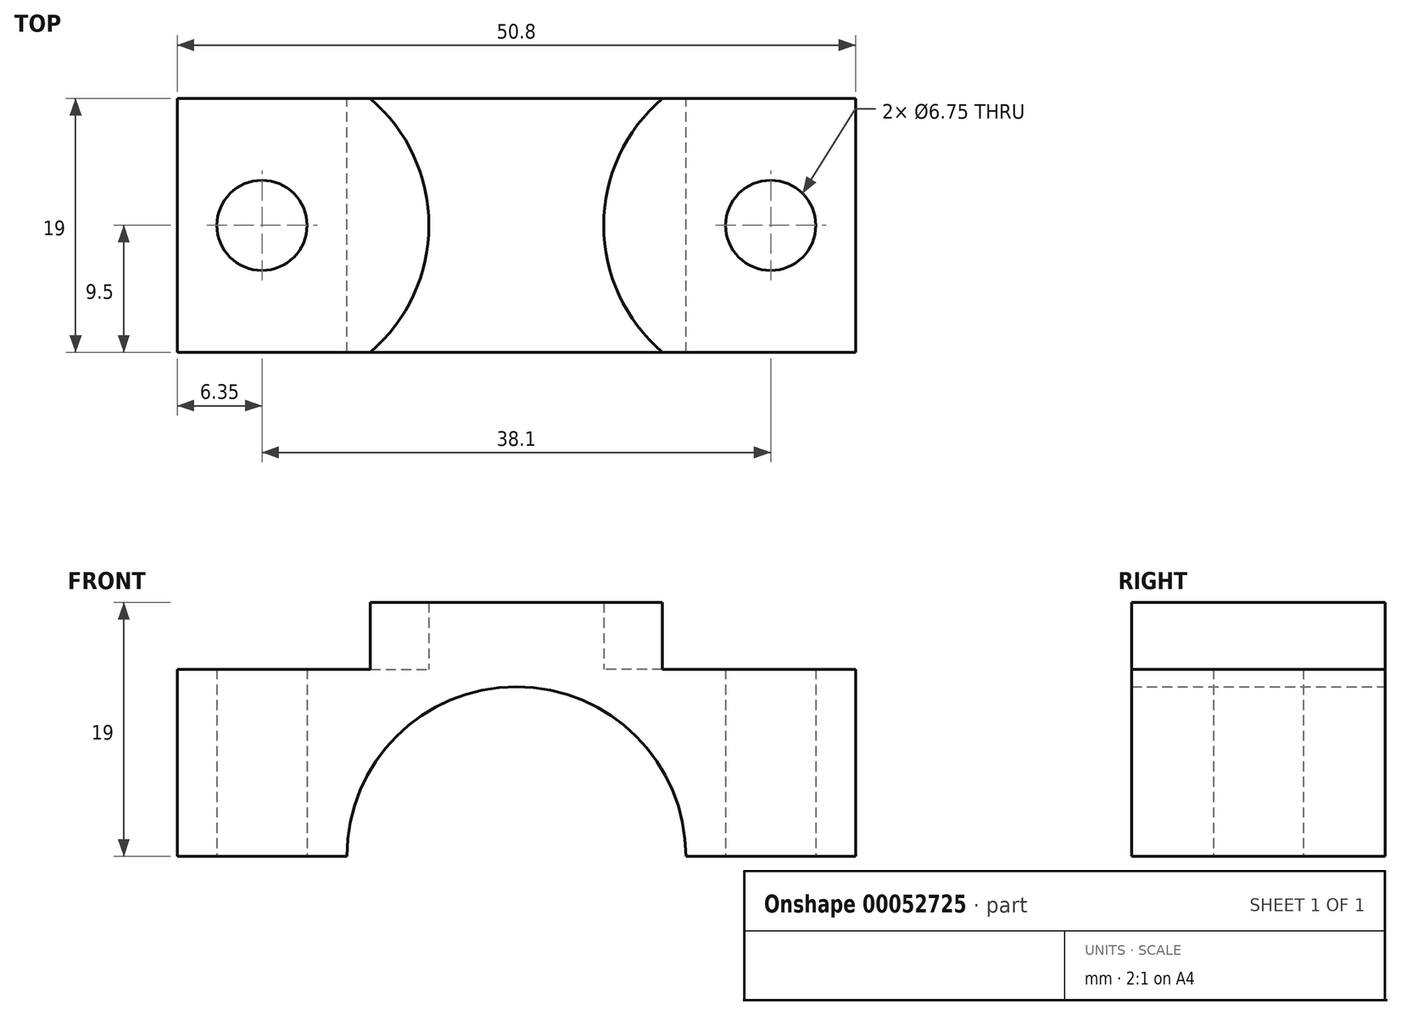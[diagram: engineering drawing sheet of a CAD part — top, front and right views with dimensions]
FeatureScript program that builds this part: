
annotation { "Feature Type Name" : "Feature", "Feature Type Description" : "" }
export const myFeature = defineFeature(function(context is Context, id is Id, definition is map)
    precondition{}
    {
        {
            var Q0;
            Q0=qCreatedBy(makeId("Front.planeOp"),FACE);
            var sketch = newSketch(context, id + "F0", { "sketchPlane" : qUnion([Q0])});
            skLineSegment(sketch, "E0.bottom", {"start": v(-25.4, 0) * mm, "end": v(25.4, 0) * mm});
            skLineSegment(sketch, "E0.top", {"start": v(-25.4, 19) * mm, "end": v(25.4, 19) * mm});
            skLineSegment(sketch, "E0.left", {"start": v(-25.4, 0) * mm, "end": v(-25.4, 19) * mm});
            skLineSegment(sketch, "E0.right", {"start": v(25.4, 0) * mm, "end": v(25.4, 19) * mm});
            skCircle(sketch, "E1", {"center": v(0, 0) * mm, "radius": 12.7 * mm});
            skSolve(sketch);
        }
        {
            var Q0;
            Q0=makeQuery(id+"F0.imprint","IMPRINT",FACE,{"disambiguationData":[TD([[makeQuery(id+"F0.imprint","IMPRINT",EDGE,{"derivedFrom":sQuery(id+"F0.wireOp",EDGE,"E0.top")}),-1.0]])]});
            extrude(context, id + "F1", {"entities" : qUnion([Q0]), "depth" : 19 * mm, "symmetric" : true});
        }
        {
            var Q0;
            {var subQ0=sQuery(id+"F0.wireOp",EDGE,"E0.bottom");Q0=makeQuery(id+"F1.opExtrude","SWEPT_FACE",FACE,{"disambiguationData":[OSD([subQ0]),TDD([makeQuery(id+"F0.imprint","IMPRINT",EDGE,{"disambiguationData":[TD([[makeQuery(id+"F0.imprint","INTERSECT",VERTEX,{"derivedFrom":[subQ0,sQuery(id+"F0.wireOp",EDGE,"E0.left")]}),-1.0]])],"derivedFrom":subQ0})])]});}
            var sketch = newSketch(context, id + "F2", { "sketchPlane" : qUnion([Q0])});
            skLineSegment(sketch, "E2", {"start": v(-25.4, 0) * mm, "end": v(-12.7, 0) * mm, "construction": true});
            skLineSegment(sketch, "E3", {"start": v(25.4, 0) * mm, "end": v(12.7, 0) * mm, "construction": true});
            skPoint(sketch, "E4", {"position": v(-19.05, 0) * mm});
            skPoint(sketch, "E5", {"position": v(19.05, 0) * mm});
            skSolve(sketch);
        }
        {
            var Q0;
            Q0=makeQuery(id+"F1.opExtrude","SWEPT_FACE",FACE,{"disambiguationData":[OSD([sQuery(id+"F0.wireOp",EDGE,"E0.top")])]});
            var sketch = newSketch(context, id + "F3", { "sketchPlane" : qUnion([Q0])});
            skPoint(sketch, "E6.0", {"position": v(-19.05, 0) * mm});
            skPoint(sketch, "E7.0", {"position": v(19.05, 0) * mm});
            skSolve(sketch);
        }
        {
            var Q0;
            Q0=sQuery(id+"F3.wireOp",VERTEX,"E7.0");
            var Q1;
            Q1=sQuery(id+"F3.wireOp",VERTEX,"E6.0");
            var Q2;
            Q2=makeQuery(id+"F1.opExtrude","SWEPT_BODY",BODY,{"disambiguationData":[OSD([sQuery(id+"F0.wireOp",EDGE,"E0.bottom"),sQuery(id+"F0.wireOp",EDGE,"E0.top"),sQuery(id+"F0.wireOp",EDGE,"E0.left"),sQuery(id+"F0.wireOp",EDGE,"E0.right"),sQuery(id+"F0.wireOp",EDGE,"E1")])]});
            hole(context, id + "F4", {"style" : HoleStyle.C_BORE, "holeDiameter" : 6.75 * mm, "cBoreDiameter" : 25 * mm, "cBoreDepth" : 5 * mm, "endStyle" : HoleEndStyle.THROUGH, "locations" : qUnion([Q0, Q1]), "scope" : qUnion([Q2])});
        }
    });
